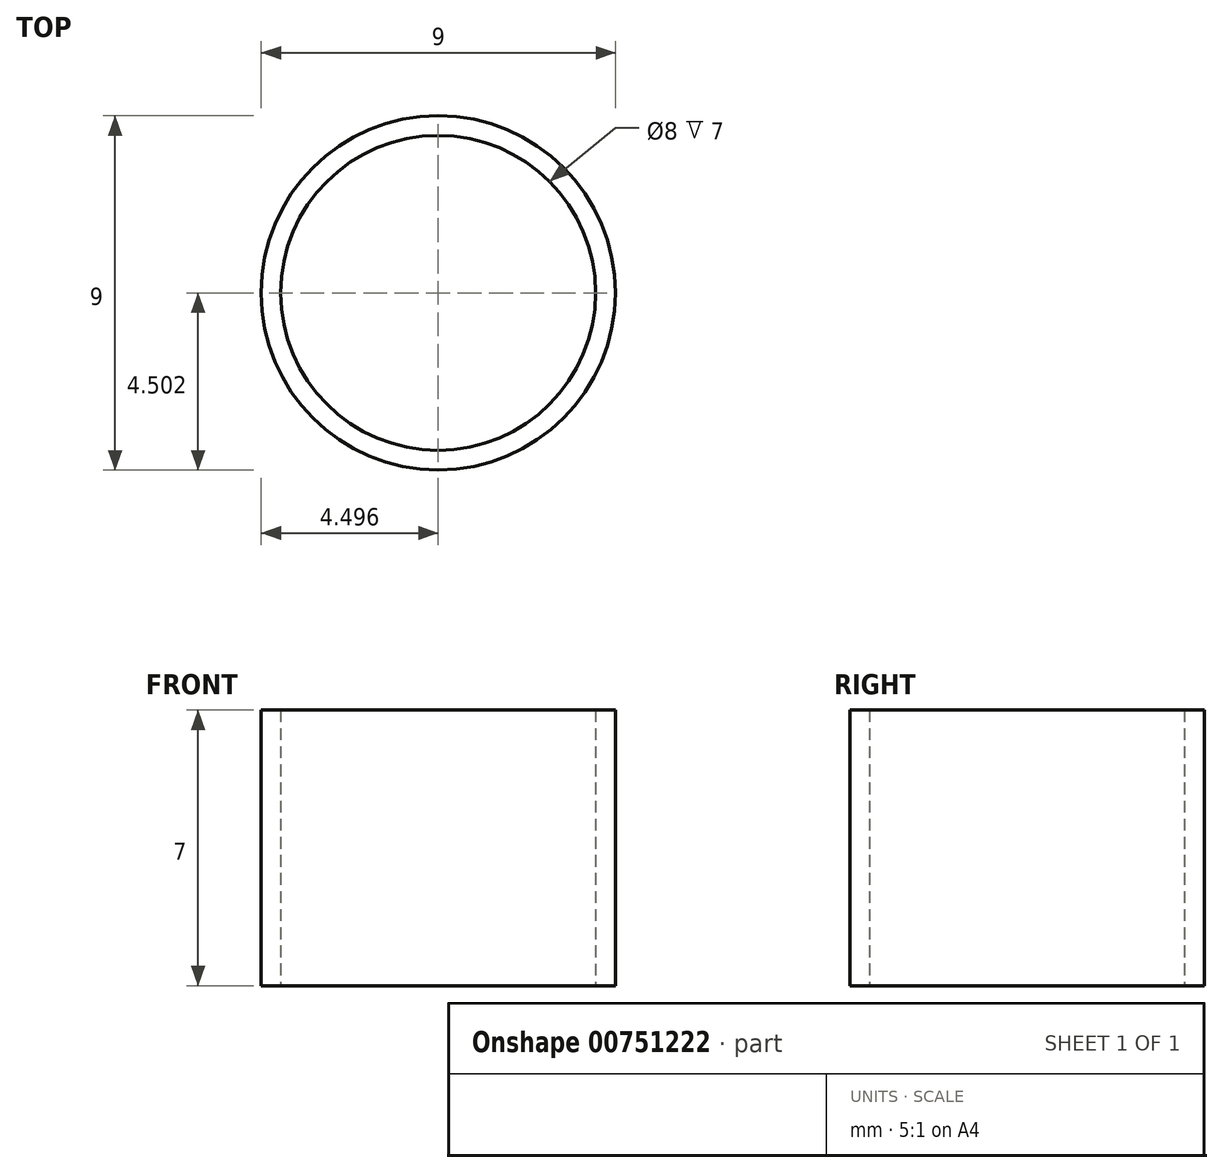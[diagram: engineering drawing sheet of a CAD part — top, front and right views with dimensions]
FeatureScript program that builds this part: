
annotation { "Feature Type Name" : "Feature", "Feature Type Description" : "" }
export const myFeature = defineFeature(function(context is Context, id is Id, definition is map)
    precondition{}
    {
        {
            var Q0;
            Q0=qCreatedBy(makeId("Top.planeOp"),FACE);
            var sketch = newSketch(context, id + "F0", { "sketchPlane" : qUnion([Q0])});
            skCircle(sketch, "E0", {"center": v(-21.97, 25.02) * mm, "radius": 4 * mm});
            skCircle(sketch, "E1", {"center": v(-21.97, 25.02) * mm, "radius": 4.5 * mm});
            skSolve(sketch);
        }
        {
            var Q0;
            Q0 = qSketchRegion(id + "F0", true);
            extrude(context, id + "F1", {"entities" : qUnion([Q0]), "depth" : 7 * mm, "offsetDistance" : 25 * mm});
        }
    });
